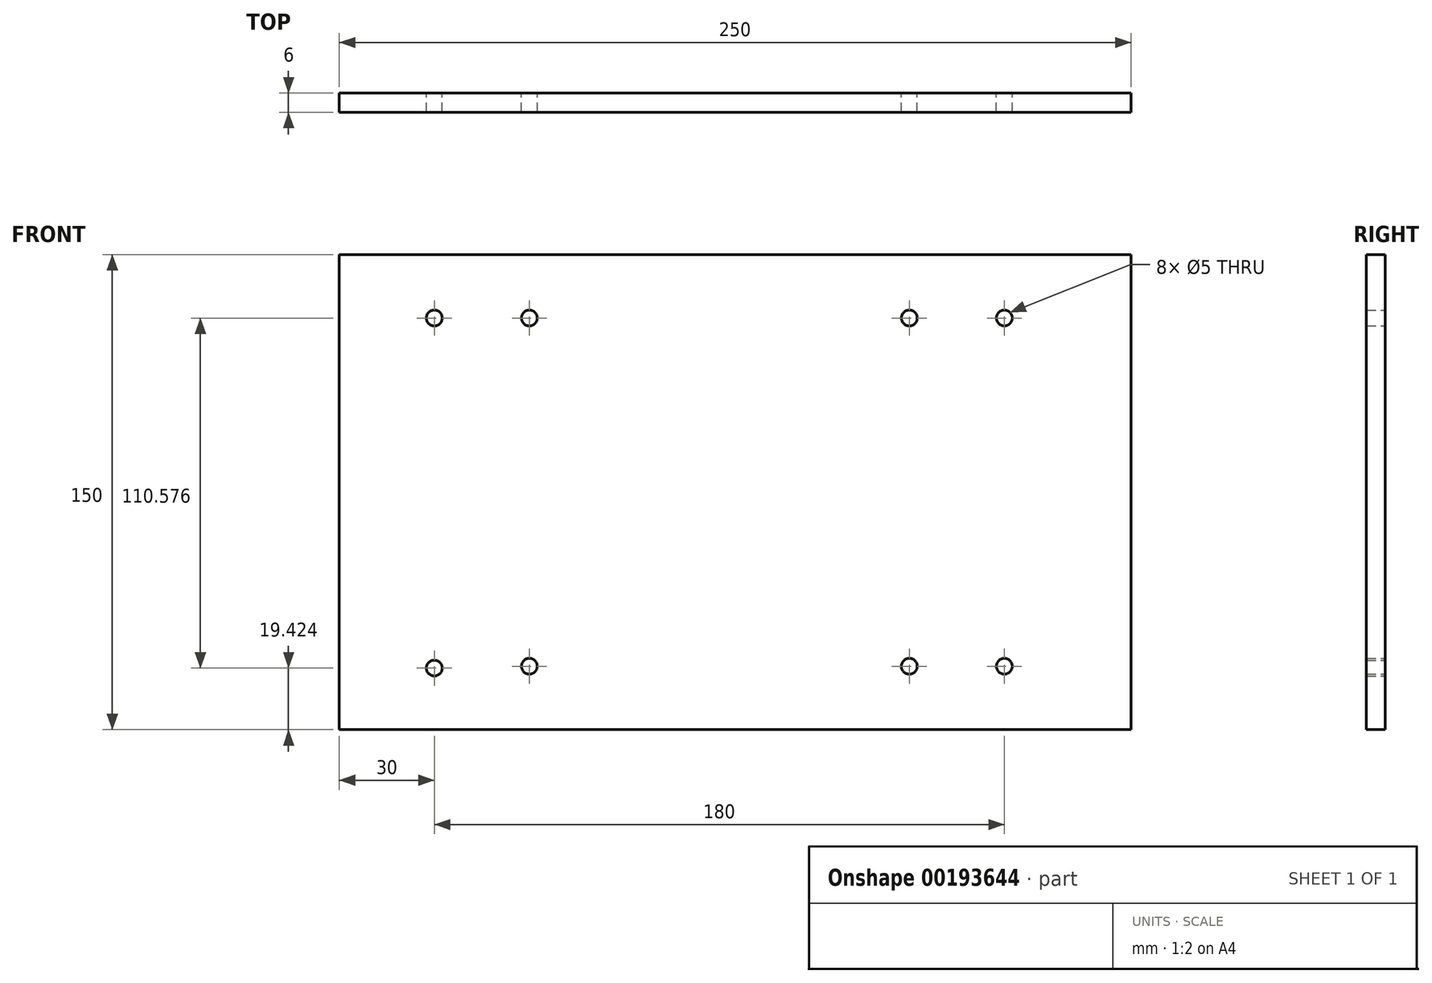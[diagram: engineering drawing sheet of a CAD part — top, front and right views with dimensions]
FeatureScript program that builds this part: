
annotation { "Feature Type Name" : "Feature", "Feature Type Description" : "" }
export const myFeature = defineFeature(function(context is Context, id is Id, definition is map)
    precondition{}
    {
        {
            var Q0;
            Q0=qCreatedBy(makeId("Front.planeOp"),FACE);
            var sketch = newSketch(context, id + "F0", { "sketchPlane" : qUnion([Q0])});
            skLineSegment(sketch, "E0.bottom", {"start": v(-125, 75) * mm, "end": v(125, 75) * mm});
            skLineSegment(sketch, "E0.top", {"start": v(-125, -75) * mm, "end": v(125, -75) * mm});
            skLineSegment(sketch, "E0.left", {"start": v(-125, 75) * mm, "end": v(-125, -75) * mm});
            skLineSegment(sketch, "E0.right", {"start": v(125, 75) * mm, "end": v(125, -75) * mm});
            skPoint(sketch, "E0.middle", {"position": v(0, 0) * mm});
            skSolve(sketch);
        }
        {
            var Q0;
            Q0=makeQuery(id+"F0.imprint","IMPRINT",FACE,{"disambiguationData":[TD([[makeQuery(id+"F0.imprint","IMPRINT",EDGE,{"derivedFrom":sQuery(id+"F0.wireOp",EDGE,"E0.bottom")}),-1.0]])]});
            var sketch = newSketch(context, id + "F1", { "sketchPlane" : qUnion([Q0])});
            skCircle(sketch, "E1", {"center": v(-95, 55) * mm, "radius": 2.5 * mm});
            skCircle(sketch, "E2", {"center": v(-65, 55) * mm, "radius": 2.5 * mm});
            skCircle(sketch, "E3", {"center": v(55, 55) * mm, "radius": 2.5 * mm});
            skCircle(sketch, "E4", {"center": v(85, 55) * mm, "radius": 2.5 * mm});
            skCircle(sketch, "E5", {"center": v(-95, -55.58) * mm, "radius": 2.5 * mm});
            skCircle(sketch, "E6", {"center": v(-65, -55) * mm, "radius": 2.5 * mm});
            skCircle(sketch, "E7", {"center": v(55, -55) * mm, "radius": 2.5 * mm});
            skCircle(sketch, "E8", {"center": v(85, -55) * mm, "radius": 2.5 * mm});
            skSolve(sketch);
        }
        {
            var Q0;
            Q0=makeQuery(id+"F1.imprint","IMPRINT",FACE,{"disambiguationData":[TD([[makeQuery(id+"F1.imprint","IMPRINT",EDGE,{"derivedFrom":sQuery(id+"F1.wireOp",EDGE,"E1")}),-1.0]])]});
            extrude(context, id + "F2", {"entities" : qUnion([Q0]), "depth" : 6 * mm});
        }
    });
